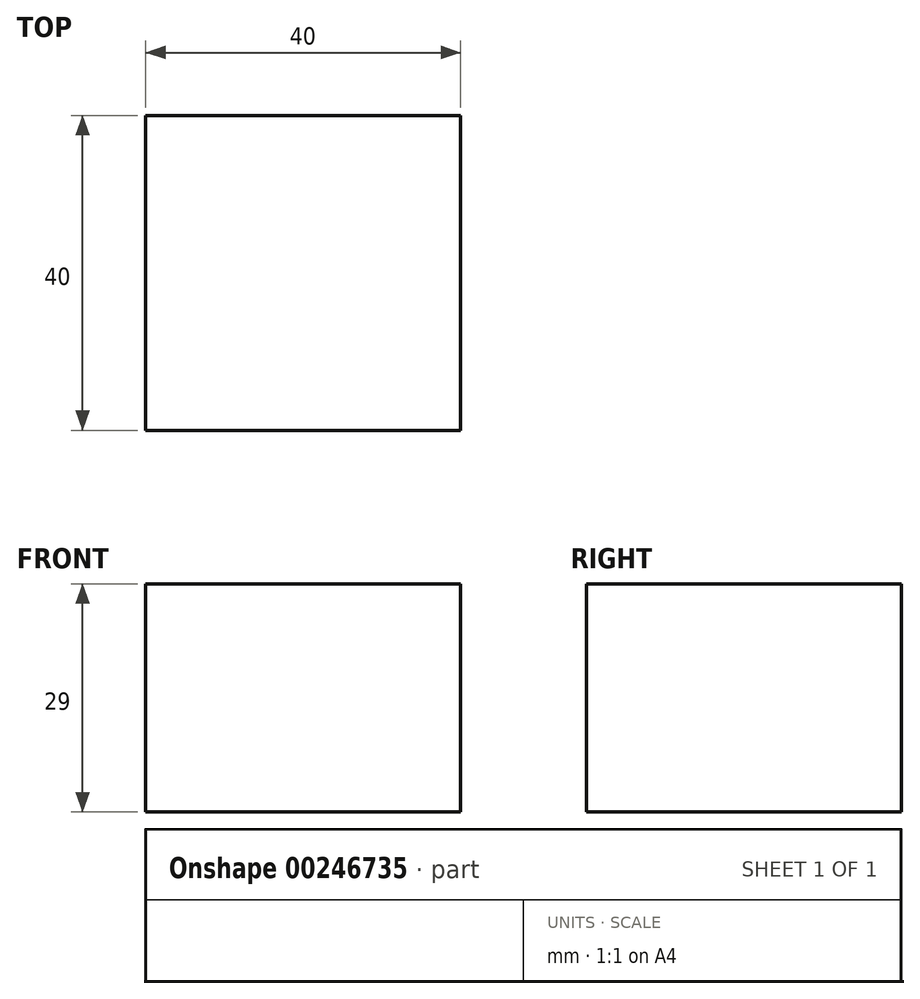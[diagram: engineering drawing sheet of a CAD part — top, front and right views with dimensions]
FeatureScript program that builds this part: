
annotation { "Feature Type Name" : "Feature", "Feature Type Description" : "" }
export const myFeature = defineFeature(function(context is Context, id is Id, definition is map)
    precondition{}
    {
        {
            var Q0;
            Q0=qCreatedBy(makeId("Top.planeOp"),FACE);
            var sketch = newSketch(context, id + "F0", { "sketchPlane" : qUnion([Q0])});
            skLineSegment(sketch, "E0", {"start": v(-18.9, 20.99) * mm, "end": v(21.1, 20.99) * mm});
            skLineSegment(sketch, "E1", {"start": v(21.1, 20.99) * mm, "end": v(21.1, -19.01) * mm});
            skLineSegment(sketch, "E2", {"start": v(21.1, -19.01) * mm, "end": v(-18.9, -19.01) * mm});
            skLineSegment(sketch, "E3", {"start": v(-18.9, -19.01) * mm, "end": v(-18.9, 20.99) * mm});
            skSolve(sketch);
        }
        {
            var Q0;
            Q0 = qSketchRegion(id + "F0", true);
            extrude(context, id + "F1", {"entities" : qUnion([Q0]), "depth" : 29 * mm});
        }
    });
